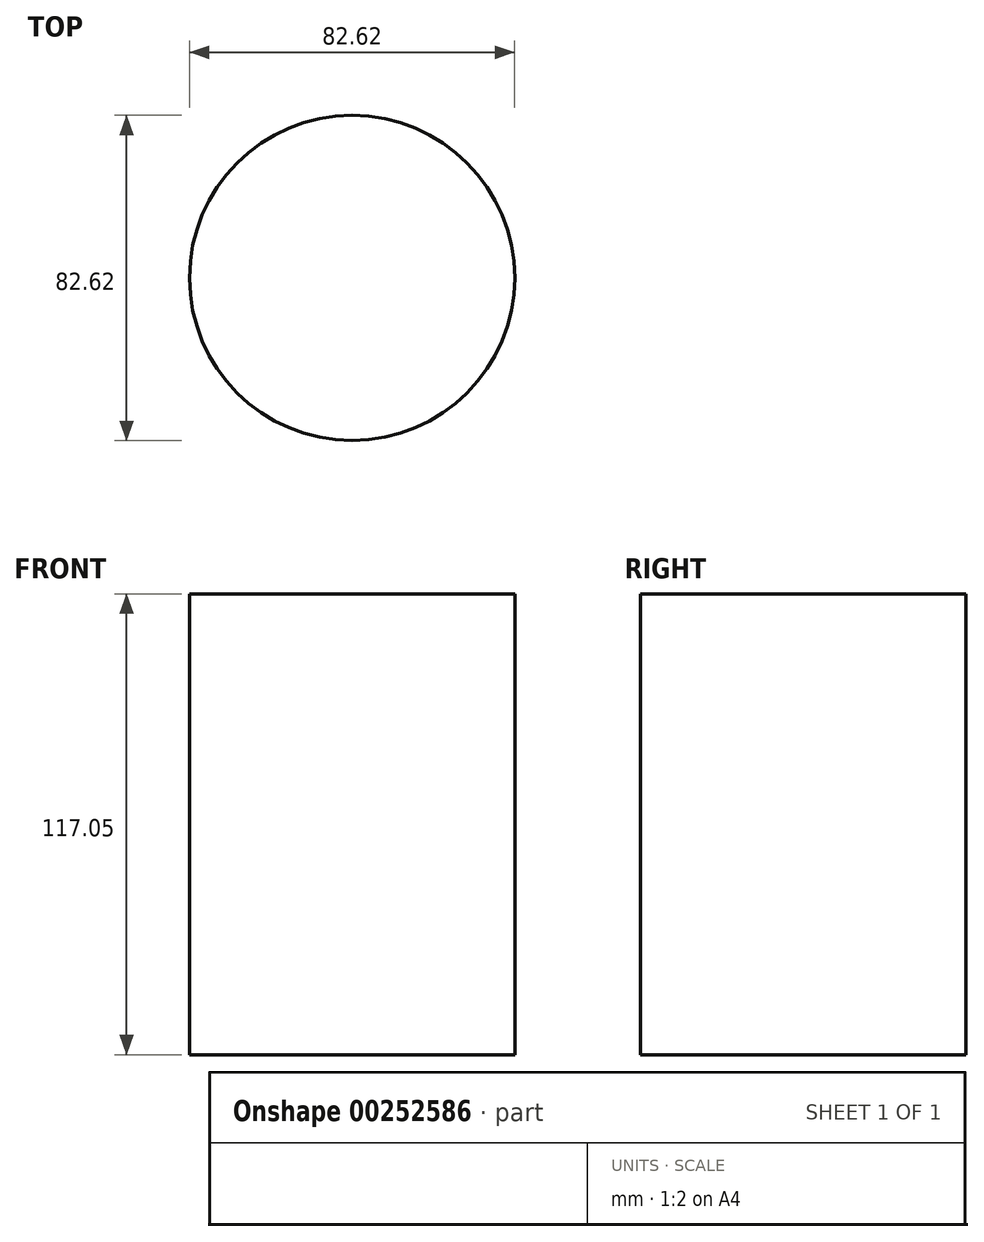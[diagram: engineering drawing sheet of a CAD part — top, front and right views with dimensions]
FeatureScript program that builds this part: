
annotation { "Feature Type Name" : "Feature", "Feature Type Description" : "" }
export const myFeature = defineFeature(function(context is Context, id is Id, definition is map)
    precondition{}
    {
        {
            var Q0;
            Q0=qCreatedBy(makeId("Front.planeOp"),FACE);
            var sketch = newSketch(context, id + "F0", { "sketchPlane" : qUnion([Q0])});
            skLineSegment(sketch, "E0.bottom", {"start": v(-41.31, 61.82) * mm, "end": v(41.31, 61.82) * mm});
            skLineSegment(sketch, "E0.top", {"start": v(-41.31, -55.23) * mm, "end": v(41.31, -55.23) * mm});
            skLineSegment(sketch, "E0.left", {"start": v(-41.31, 61.82) * mm, "end": v(-41.31, -55.23) * mm});
            skLineSegment(sketch, "E0.right", {"start": v(41.31, 61.82) * mm, "end": v(41.31, -55.23) * mm});
            skLineSegment(sketch, "E1", {"start": v(0, 61.82) * mm, "end": v(0, -55.23) * mm});
            skSolve(sketch);
        }
        {
            var Q0;
            {var subQ0=sQuery(id+"F0.wireOp",EDGE,"E0.left");Q0=makeQuery(id+"F0.imprint","IMPRINT",FACE,{"disambiguationData":[TD([[makeQuery(id+"F0.imprint","IMPRINT",EDGE,{"derivedFrom":subQ0}),1.0]])]});}
            var Q1;
            Q1=sQuery(id+"F0.wireOp",EDGE,"E1");
            revolve(context, id + "F1", {"entities" : qUnion([Q0]), "axis" : qUnion([Q1]), "revolveType" : RevolveType.FULL});
        }
    });
